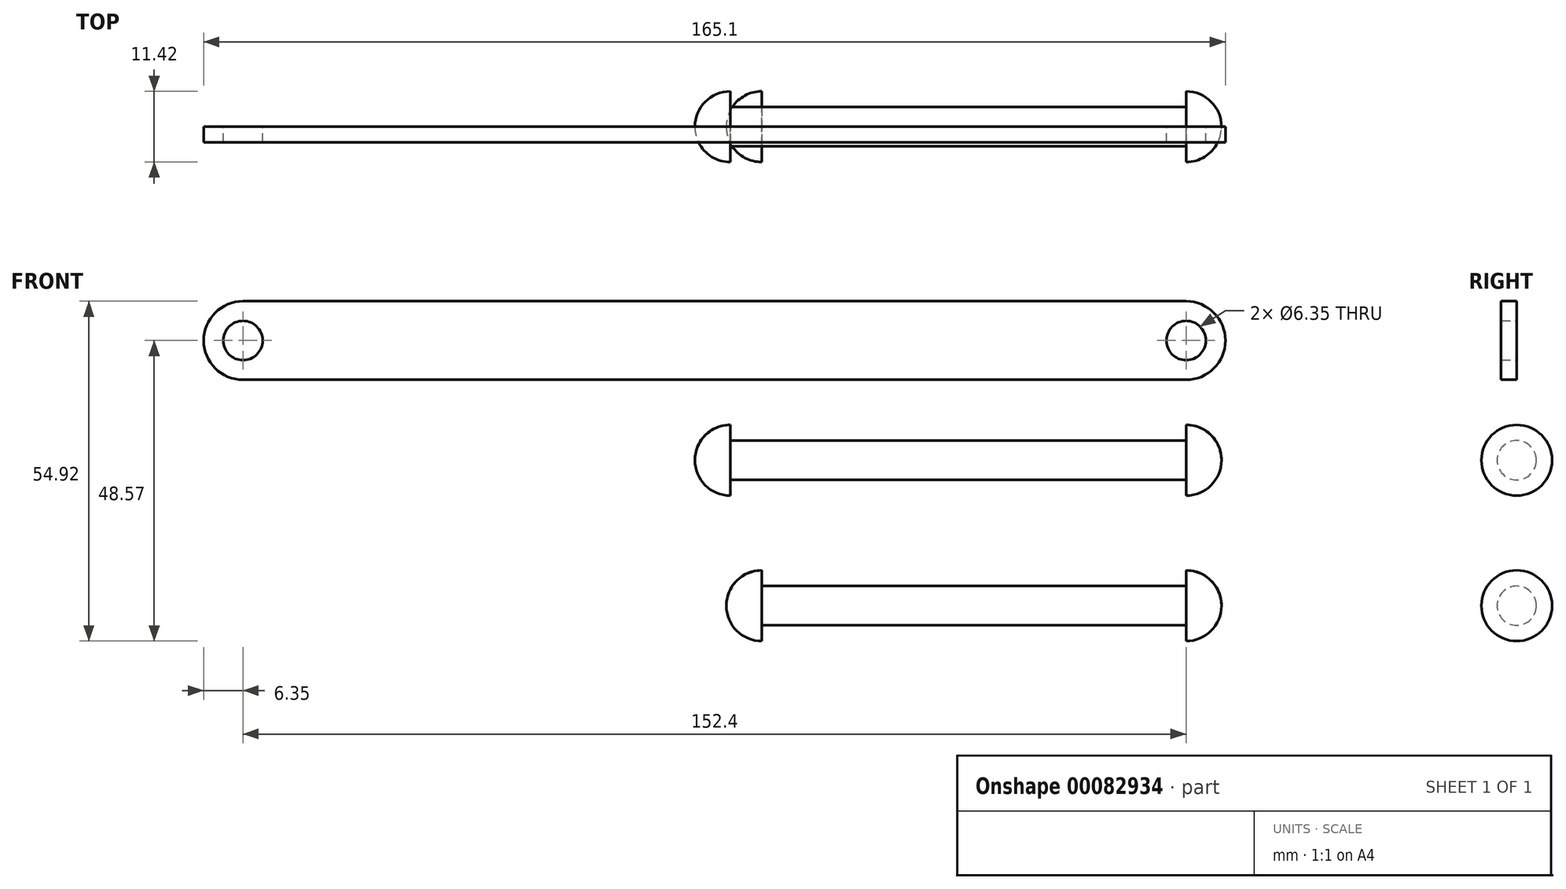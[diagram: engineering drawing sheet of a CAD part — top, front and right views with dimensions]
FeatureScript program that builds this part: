
annotation { "Feature Type Name" : "Feature", "Feature Type Description" : "" }
export const myFeature = defineFeature(function(context is Context, id is Id, definition is map)
    precondition{}
    {
        {
            var Q0;
            Q0=qCreatedBy(makeId("Front.planeOp"),FACE);
            var sketch = newSketch(context, id + "F0", { "sketchPlane" : qUnion([Q0])});
            skLineSegment(sketch, "E0.bottom", {"start": v(0, 0) * mm, "end": v(-152.4, 0) * mm});
            skLineSegment(sketch, "E0.top", {"start": v(0, 12.7) * mm, "end": v(-152.4, 12.7) * mm});
            skLineSegment(sketch, "E0.left", {"start": v(0, 0) * mm, "end": v(0, 12.7) * mm});
            skLineSegment(sketch, "E0.right", {"start": v(-152.4, 0) * mm, "end": v(-152.4, 12.7) * mm});
            skArc(sketch, "E1", {"start": v(-152.4, 12.7) * mm, "mid": v(-158.75, 6.35) * mm, "end": v(-152.4, 0) * mm});
            skArc(sketch, "E2", {"start": v(0, 0) * mm, "mid": v(6.35, 6.35) * mm, "end": v(0, 12.7) * mm});
            skCircle(sketch, "E3", {"center": v(-152.4, 6.35) * mm, "radius": 3.18 * mm});
            skCircle(sketch, "E4", {"center": v(0, 6.35) * mm, "radius": 3.18 * mm});
            skSolve(sketch);
        }
        {
            var Q0;
            {var subQ0=sQuery(id+"F0.wireOp",EDGE,"E2");Q0=makeQuery(id+"F0.imprint","IMPRINT",FACE,{"disambiguationData":[TD([[makeQuery(id+"F0.imprint","IMPRINT",EDGE,{"derivedFrom":subQ0}),1.0]])]});}
            var Q1;
            {var subQ5=sQuery(id+"F0.wireOp",EDGE,"E0.bottom");Q1=makeQuery(id+"F0.imprint","IMPRINT",FACE,{"disambiguationData":[TD([[makeQuery(id+"F0.imprint","IMPRINT",EDGE,{"derivedFrom":subQ5}),-1.0]])]});}
            var Q2;
            {var subQ0=sQuery(id+"F0.wireOp",EDGE,"E1");Q2=makeQuery(id+"F0.imprint","IMPRINT",FACE,{"disambiguationData":[TD([[makeQuery(id+"F0.imprint","IMPRINT",EDGE,{"derivedFrom":subQ0}),1.0]])]});}
            extrude(context, id + "F1", {"entities" : qUnion([Q0, Q1, Q2]), "depth" : 2.54 * mm});
        }
        {
            var Q0;
            Q0=qCreatedBy(makeId("Front.planeOp"),FACE);
            var sketch = newSketch(context, id + "F2", { "sketchPlane" : qUnion([Q0])});
            skLineSegment(sketch, "E5.bottom", {"start": v(0, -9.82) * mm, "end": v(-73.66, -9.82) * mm});
            skLineSegment(sketch, "E5.top", {"start": v(0, -13) * mm, "end": v(-73.66, -13) * mm});
            skLineSegment(sketch, "E5.left", {"start": v(0, -9.82) * mm, "end": v(0, -13) * mm});
            skLineSegment(sketch, "E5.right", {"start": v(-73.66, -9.82) * mm, "end": v(-73.66, -13) * mm});
            skLineSegment(sketch, "E6", {"start": v(0, -13) * mm, "end": v(-95.26, -13) * mm, "construction": true});
            skLineSegment(sketch, "E7", {"start": v(-95.26, -13) * mm, "end": v(15.12, -13) * mm, "construction": true});
            skArc(sketch, "E8", {"start": v(-73.66, -7.28) * mm, "mid": v(-77.7, -8.95) * mm, "end": v(-79.38, -13) * mm});
            skLineSegment(sketch, "E9", {"start": v(-73.66, -7.28) * mm, "end": v(-73.66, -9.82) * mm});
            skLineSegment(sketch, "E10", {"start": v(0, -9.82) * mm, "end": v(0, -7.28) * mm});
            skLineSegment(sketch, "E11", {"start": v(-73.66, -13) * mm, "end": v(-79.38, -13) * mm});
            skLineSegment(sketch, "E12", {"start": v(0, -13) * mm, "end": v(5.72, -13) * mm});
            skArc(sketch, "E13", {"start": v(0, -7.28) * mm, "mid": v(4.04, -8.95) * mm, "end": v(5.72, -13) * mm});
            skSolve(sketch);
        }
        {
            var Q0;
            Q0 = qSketchRegion(id + "F2", true);
            var Q1;
            Q1=sQuery(id+"F2.wireOp",EDGE,"E7");
            revolve(context, id + "F3", {"entities" : qUnion([Q0]), "axis" : qUnion([Q1]), "revolveType" : RevolveType.FULL});
        }
        {
            var Q0;
            Q0=qCreatedBy(makeId("Front.planeOp"),FACE);
            var sketch = newSketch(context, id + "F4", { "sketchPlane" : qUnion([Q0])});
            skLineSegment(sketch, "E14.bottom", {"start": v(0, -33.33) * mm, "end": v(-68.58, -33.33) * mm});
            skLineSegment(sketch, "E14.top", {"start": v(0, -36.5) * mm, "end": v(-68.58, -36.5) * mm});
            skLineSegment(sketch, "E14.left", {"start": v(0, -33.33) * mm, "end": v(0, -36.5) * mm});
            skLineSegment(sketch, "E14.right", {"start": v(-68.58, -33.33) * mm, "end": v(-68.58, -36.5) * mm});
            skLineSegment(sketch, "E15", {"start": v(-74.3, -36.5) * mm, "end": v(5.71, -36.5) * mm});
            skLineSegment(sketch, "E16", {"start": v(-96.72, -36.5) * mm, "end": v(28.13, -36.5) * mm, "construction": true});
            skArc(sketch, "E17", {"start": v(-74.3, -36.5) * mm, "mid": v(-72.62, -32.47) * mm, "end": v(-68.58, -30.8) * mm});
            skArc(sketch, "E18", {"start": v(5.72, -36.5) * mm, "mid": v(4.04, -32.47) * mm, "end": v(0, -30.8) * mm});
            skLineSegment(sketch, "E19", {"start": v(-68.58, -30.8) * mm, "end": v(-68.58, -33.33) * mm});
            skLineSegment(sketch, "E20", {"start": v(0, -30.8) * mm, "end": v(0, -33.33) * mm});
            skSolve(sketch);
        }
        {
            var Q0;
            Q0 = qSketchRegion(id + "F4", true);
            var Q1;
            Q1=sQuery(id+"F4.wireOp",EDGE,"E16");
            revolve(context, id + "F5", {"entities" : qUnion([Q0]), "axis" : qUnion([Q1]), "revolveType" : RevolveType.FULL});
        }
    });
